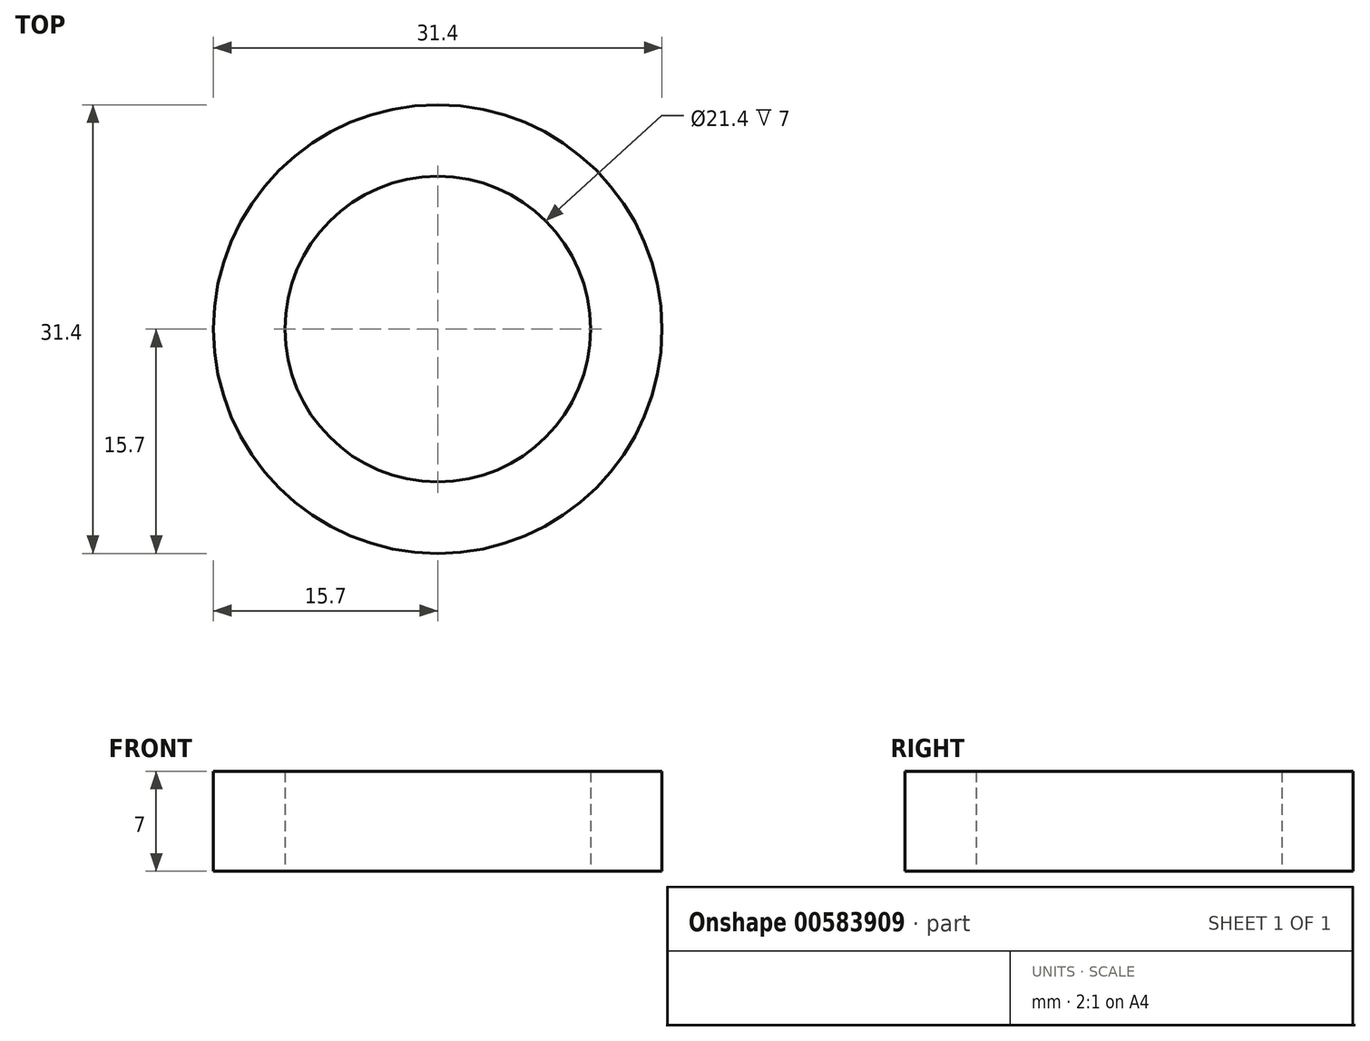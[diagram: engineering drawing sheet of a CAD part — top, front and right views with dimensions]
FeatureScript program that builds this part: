
annotation { "Feature Type Name" : "Feature", "Feature Type Description" : "" }
export const myFeature = defineFeature(function(context is Context, id is Id, definition is map)
    precondition{}
    {
        {
            var Q0;
            Q0=qCreatedBy(makeId("Top.planeOp"),FACE);
            var sketch = newSketch(context, id + "F0", { "sketchPlane" : qUnion([Q0])});
            skCircle(sketch, "E0", {"center": v(0, 0) * mm, "radius": 10.7 * mm});
            skCircle(sketch, "E1", {"center": v(0, 0) * mm, "radius": 15.7 * mm});
            skSolve(sketch);
        }
        {
            var Q0;
            Q0 = qSketchRegion(id + "F0", true);
            extrude(context, id + "F1", {"entities" : qUnion([Q0]), "depth" : 7 * mm, "offsetDistance" : 25.4 * mm});
        }
    });
